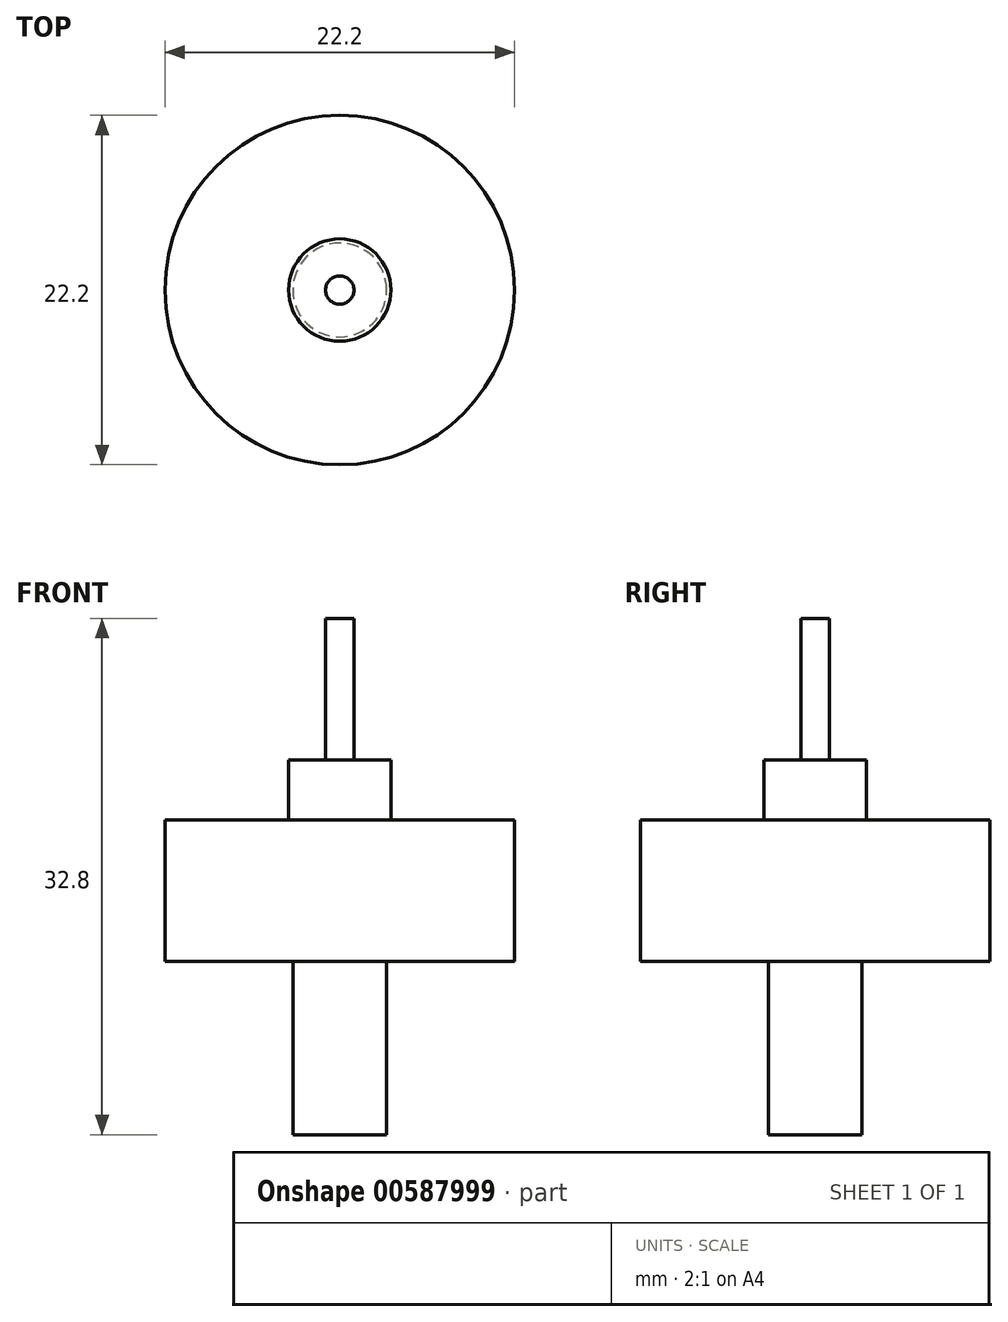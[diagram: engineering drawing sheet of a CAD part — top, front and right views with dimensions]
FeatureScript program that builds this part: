
annotation { "Feature Type Name" : "Feature", "Feature Type Description" : "" }
export const myFeature = defineFeature(function(context is Context, id is Id, definition is map)
    precondition{}
    {
        {
            var Q0;
            Q0=qCreatedBy(makeId("Front.planeOp"),FACE);
            var sketch = newSketch(context, id + "F0", { "sketchPlane" : qUnion([Q0])});
            skLineSegment(sketch, "E0", {"start": v(0, 0) * mm, "end": v(-2.98, 0) * mm});
            skLineSegment(sketch, "E1", {"start": v(-2.98, 0) * mm, "end": v(-2.98, 11) * mm});
            skLineSegment(sketch, "E2", {"start": v(0, 11) * mm, "end": v(0, 0) * mm});
            skLineSegment(sketch, "E3.bottom", {"start": v(-2.98, 11) * mm, "end": v(-11.1, 11) * mm});
            skLineSegment(sketch, "E3.top", {"start": v(-3.25, 20) * mm, "end": v(-11.1, 20) * mm});
            skLineSegment(sketch, "E3.left", {"start": v(0, 11) * mm, "end": v(0, 20) * mm});
            skLineSegment(sketch, "E3.right", {"start": v(-11.1, 11) * mm, "end": v(-11.1, 20) * mm});
            skLineSegment(sketch, "E4.top", {"start": v(-0.9, 23.8) * mm, "end": v(-3.25, 23.8) * mm});
            skLineSegment(sketch, "E4.left", {"start": v(0, 20) * mm, "end": v(0, 23.8) * mm});
            skLineSegment(sketch, "E4.right", {"start": v(-3.25, 20) * mm, "end": v(-3.25, 23.8) * mm});
            skLineSegment(sketch, "E5.top", {"start": v(0, 32.8) * mm, "end": v(-0.9, 32.8) * mm});
            skLineSegment(sketch, "E5.left", {"start": v(0, 23.8) * mm, "end": v(0, 32.8) * mm});
            skLineSegment(sketch, "E5.right", {"start": v(-0.9, 23.8) * mm, "end": v(-0.9, 32.8) * mm});
            skLineSegment(sketch, "E6", {"start": v(0, 0) * mm, "end": v(0, -8.6) * mm});
            skSolve(sketch);
        }
        {
            var Q0;
            Q0=makeQuery(id+"F0.imprint","IMPRINT",FACE,{"disambiguationData":[TD([[makeQuery(id+"F0.imprint","IMPRINT",EDGE,{"derivedFrom":sQuery(id+"F0.wireOp",EDGE,"E0")}),-1.0]])]});
            var Q1;
            Q1=sQuery(id+"F0.wireOp",EDGE,"E6");
            revolve(context, id + "F1", {"entities" : qUnion([Q0]), "axis" : qUnion([Q1]), "revolveType" : RevolveType.FULL});
        }
    });
